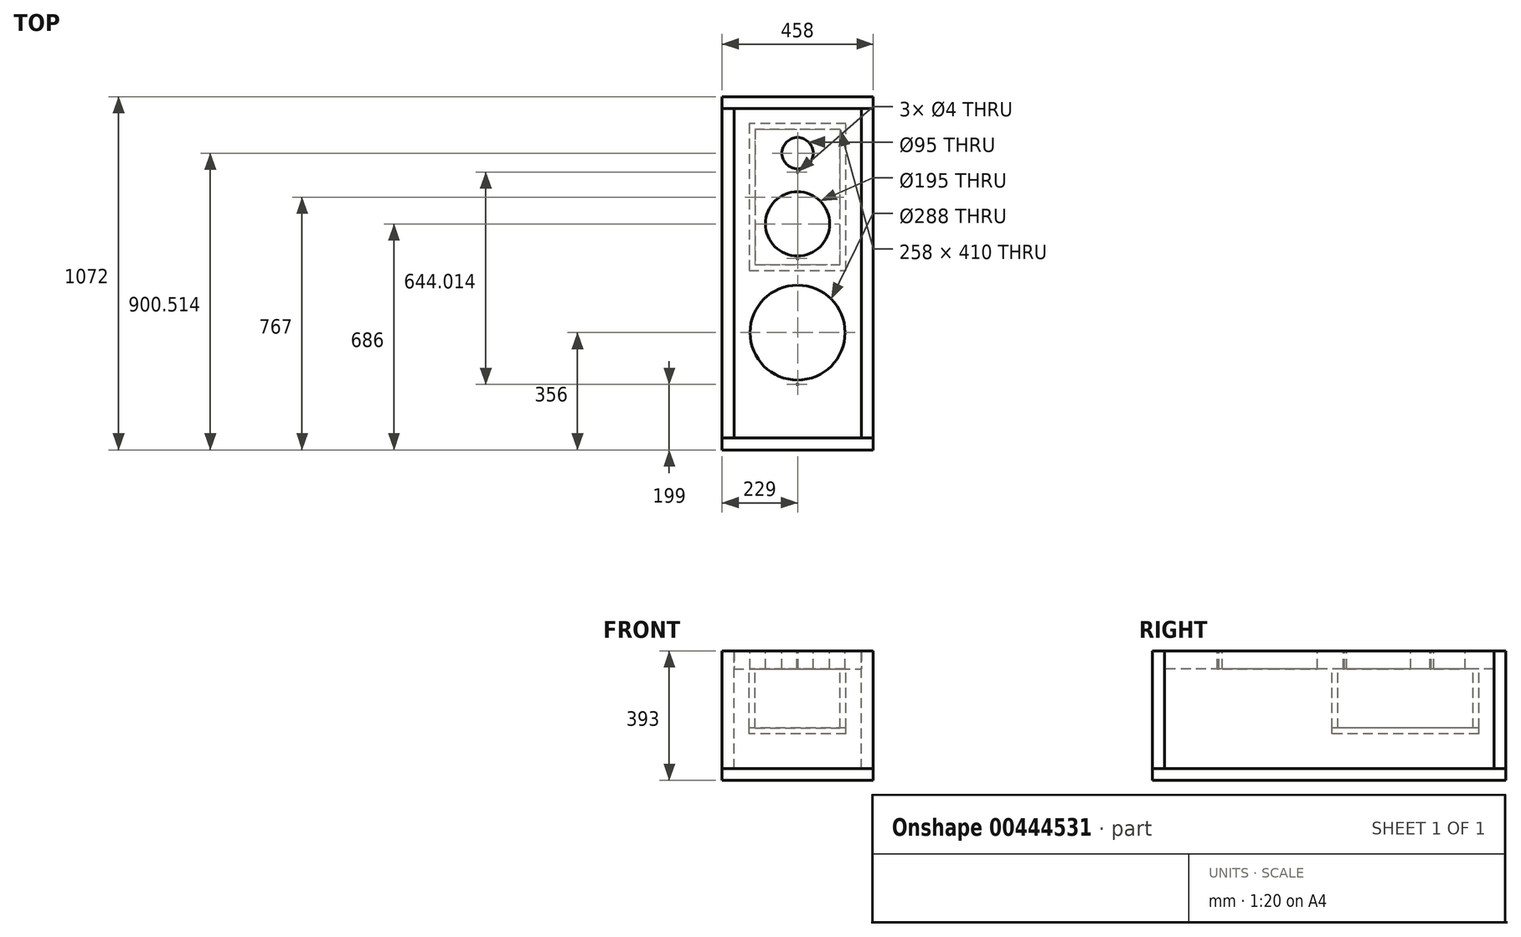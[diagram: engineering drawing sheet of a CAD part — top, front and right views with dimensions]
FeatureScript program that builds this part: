
annotation { "Feature Type Name" : "Feature", "Feature Type Description" : "" }
export const myFeature = defineFeature(function(context is Context, id is Id, definition is map)
    precondition{}
    {
        {
            var Q0;
            Q0=qCreatedBy(makeId("Top.planeOp"),FACE);
            var sketch = newSketch(context, id + "F0", { "sketchPlane" : qUnion([Q0])});
            skLineSegment(sketch, "E0.bottom", {"start": v(-193, 500) * mm, "end": v(193, 500) * mm});
            skLineSegment(sketch, "E0.top", {"start": v(-193, -500) * mm, "end": v(193, -500) * mm});
            skLineSegment(sketch, "E0.left", {"start": v(-193, 500) * mm, "end": v(-193, -500) * mm});
            skLineSegment(sketch, "E0.right", {"start": v(193, 500) * mm, "end": v(193, -500) * mm});
            skPoint(sketch, "E0.middle", {"position": v(0, 0) * mm});
            skSolve(sketch);
        }
        {
            var Q0;
            Q0 = qSketchRegion(id + "F0", true);
            extrude(context, id + "F1", {"entities" : qUnion([Q0]), "depth" : 54 * mm});
        }
        {
            var Q0;
            Q0=makeQuery(id+"F1.opExtrude","CAP_FACE",FACE,{"disambiguationData":[OSD([sQuery(id+"F0.wireOp",EDGE,"E0.bottom"),sQuery(id+"F0.wireOp",EDGE,"E0.top"),sQuery(id+"F0.wireOp",EDGE,"E0.left"),sQuery(id+"F0.wireOp",EDGE,"E0.right")])],"isStart":false});
            var sketch = newSketch(context, id + "F2", { "sketchPlane" : qUnion([Q0])});
            skCircle(sketch, "E1", {"center": v(0, -180) * mm, "radius": 144 * mm});
            skCircle(sketch, "E2", {"center": v(0, 150) * mm, "radius": 97.5 * mm});
            skCircle(sketch, "E3", {"center": v(0, 364.51) * mm, "radius": 47.5 * mm});
            skSolve(sketch);
        }
        {
            var Q0;
            Q0 = qSketchRegion(id + "F2", true);
            extrude(context, id + "F3", {"entities" : qUnion([Q0]), "operationType" : NewBodyOperationType.REMOVE, "oppositeDirection" : true, "depth" : 80 * mm});
        }
        {
            var Q0;
            Q0=makeQuery(id+"F1.opExtrude","SWEPT_FACE",FACE,{"disambiguationData":[OSD([sQuery(id+"F0.wireOp",EDGE,"E0.left")])]});
            var sketch = newSketch(context, id + "F4", { "sketchPlane" : qUnion([Q0])});
            skLineSegment(sketch, "E4", {"start": v(-500, 54) * mm, "end": v(-500, -303) * mm});
            skLineSegment(sketch, "E5", {"start": v(-500, -303) * mm, "end": v(500, -303) * mm});
            skLineSegment(sketch, "E6", {"start": v(500, -303) * mm, "end": v(500, 54) * mm});
            skLineSegment(sketch, "E7", {"start": v(500, 54) * mm, "end": v(-500, 54) * mm});
            skSolve(sketch);
        }
        {
            var Q0;
            Q0 = qSketchRegion(id + "F4", true);
            extrude(context, id + "F5", {"entities" : qUnion([Q0]), "depth" : 36 * mm});
        }
        {
            var Q0;
            Q0=makeQuery(id+"F1.opExtrude","SWEPT_FACE",FACE,{"disambiguationData":[OSD([sQuery(id+"F0.wireOp",EDGE,"E0.right")])]});
            var sketch = newSketch(context, id + "F6", { "sketchPlane" : qUnion([Q0])});
            skLineSegment(sketch, "E8", {"start": v(-500, 54) * mm, "end": v(-500, -303) * mm});
            skPoint(sketch, "E8.endSnap0", {"position": v(-500, 27) * mm});
            skLineSegment(sketch, "E9", {"start": v(-500, -303) * mm, "end": v(500, -303) * mm});
            skLineSegment(sketch, "E10", {"start": v(500, -303) * mm, "end": v(500, 54) * mm});
            skLineSegment(sketch, "E11", {"start": v(500, 54) * mm, "end": v(-500, 54) * mm});
            skSolve(sketch);
        }
        {
            var Q0;
            Q0 = qSketchRegion(id + "F6", true);
            extrude(context, id + "F7", {"entities" : qUnion([Q0]), "depth" : 36 * mm});
        }
        {
            var Q0;
            Q0=makeQuery(id+"F1.opExtrude","CAP_FACE",FACE,{"disambiguationData":[OSD([sQuery(id+"F0.wireOp",EDGE,"E0.bottom"),sQuery(id+"F0.wireOp",EDGE,"E0.top"),sQuery(id+"F0.wireOp",EDGE,"E0.left"),sQuery(id+"F0.wireOp",EDGE,"E0.right")])],"isStart":true});
            var sketch = newSketch(context, id + "F8", { "sketchPlane" : qUnion([Q0])});
            skLineSegment(sketch, "E12", {"start": v(-129, -26) * mm, "end": v(129, -26) * mm});
            skLineSegment(sketch, "E13", {"start": v(129, -26) * mm, "end": v(129, -436) * mm});
            skLineSegment(sketch, "E14", {"start": v(129, -436) * mm, "end": v(-129, -436) * mm});
            skLineSegment(sketch, "E15", {"start": v(-129, -436) * mm, "end": v(-129, -26) * mm});
            skLineSegment(sketch, "E16.0", {"start": v(-147, -454) * mm, "end": v(-147, -8) * mm});
            skLineSegment(sketch, "E16.1", {"start": v(147, -454) * mm, "end": v(-147, -454) * mm});
            skLineSegment(sketch, "E16.2", {"start": v(147, -8) * mm, "end": v(147, -454) * mm});
            skLineSegment(sketch, "E16.3", {"start": v(-147, -8) * mm, "end": v(147, -8) * mm});
            skSolve(sketch);
        }
        {
            var Q0;
            Q0=makeQuery(id+"F8.imprint","IMPRINT",FACE,{"disambiguationData":[TD([[makeQuery(id+"F8.imprint","IMPRINT",EDGE,{"derivedFrom":sQuery(id+"F8.wireOp",EDGE,"E12")}),1.0]])]});
            extrude(context, id + "F9", {"entities" : qUnion([Q0]), "depth" : 180 * mm});
        }
        {
            var Q0;
            Q0=makeQuery(id+"F9.opExtrude","CAP_FACE",FACE,{"disambiguationData":[OSD([sQuery(id+"F8.wireOp",EDGE,"E12"),sQuery(id+"F8.wireOp",EDGE,"E13"),sQuery(id+"F8.wireOp",EDGE,"E14"),sQuery(id+"F8.wireOp",EDGE,"E15"),sQuery(id+"F8.wireOp",EDGE,"E16.0"),sQuery(id+"F8.wireOp",EDGE,"E16.1"),sQuery(id+"F8.wireOp",EDGE,"E16.2"),sQuery(id+"F8.wireOp",EDGE,"E16.3")])],"isStart":false});
            var sketch = newSketch(context, id + "F10", { "sketchPlane" : qUnion([Q0])});
            skLineSegment(sketch, "E17", {"start": v(-147, -8) * mm, "end": v(147, -8) * mm});
            skLineSegment(sketch, "E18", {"start": v(147, -8) * mm, "end": v(147, -454) * mm});
            skLineSegment(sketch, "E19", {"start": v(147, -454) * mm, "end": v(-147, -454) * mm});
            skLineSegment(sketch, "E20", {"start": v(-147, -454) * mm, "end": v(-147, -8) * mm});
            skSolve(sketch);
        }
        {
            var Q0;
            Q0 = qSketchRegion(id + "F10", true);
            extrude(context, id + "F11", {"entities" : qUnion([Q0]), "depth" : 18 * mm});
        }
        {
            var Q0;
            Q0=makeQuery(id+"F1.opExtrude","SWEPT_FACE",FACE,{"disambiguationData":[OSD([sQuery(id+"F0.wireOp",EDGE,"E0.bottom")])]});
            var sketch = newSketch(context, id + "F12", { "sketchPlane" : qUnion([Q0])});
            skLineSegment(sketch, "E21", {"start": v(-229, 54) * mm, "end": v(229, 54) * mm});
            skLineSegment(sketch, "E22", {"start": v(229, 54) * mm, "end": v(229, -303) * mm});
            skLineSegment(sketch, "E23", {"start": v(229, -303) * mm, "end": v(-229, -303) * mm});
            skLineSegment(sketch, "E24", {"start": v(-229, -303) * mm, "end": v(-229, 54) * mm});
            skSolve(sketch);
        }
        {
            var Q0;
            Q0 = qSketchRegion(id + "F12", true);
            extrude(context, id + "F13", {"entities" : qUnion([Q0]), "depth" : 36 * mm});
        }
        {
            var Q0;
            Q0=makeQuery(id+"F1.opExtrude","SWEPT_FACE",FACE,{"disambiguationData":[OSD([sQuery(id+"F0.wireOp",EDGE,"E0.top")])]});
            var sketch = newSketch(context, id + "F14", { "sketchPlane" : qUnion([Q0])});
            skLineSegment(sketch, "E25", {"start": v(-229, 54) * mm, "end": v(229, 54) * mm});
            skLineSegment(sketch, "E26", {"start": v(229, 54) * mm, "end": v(229, -303) * mm});
            skLineSegment(sketch, "E27", {"start": v(229, -303) * mm, "end": v(-229, -303) * mm});
            skLineSegment(sketch, "E28", {"start": v(-229, -303) * mm, "end": v(-229, 54) * mm});
            skSolve(sketch);
        }
        {
            var Q0;
            Q0 = qSketchRegion(id + "F14", true);
            extrude(context, id + "F15", {"entities" : qUnion([Q0]), "depth" : 36 * mm});
        }
        {
            var Q0;
            Q0=makeQuery(id+"F15.opExtrude","SWEPT_FACE",FACE,{"disambiguationData":[OSD([sQuery(id+"F14.wireOp",EDGE,"E27")])]});
            var sketch = newSketch(context, id + "F16", { "sketchPlane" : qUnion([Q0])});
            skLineSegment(sketch, "E29", {"start": v(-229, 536) * mm, "end": v(229, 536) * mm});
            skLineSegment(sketch, "E30", {"start": v(229, 536) * mm, "end": v(229, -536) * mm});
            skLineSegment(sketch, "E31", {"start": v(229, -536) * mm, "end": v(-229, -536) * mm});
            skLineSegment(sketch, "E32", {"start": v(-229, -536) * mm, "end": v(-229, 536) * mm});
            skSolve(sketch);
        }
        {
            var Q0;
            Q0 = qSketchRegion(id + "F16", true);
            extrude(context, id + "F17", {"entities" : qUnion([Q0]), "depth" : 36 * mm});
        }
        {
            var Q0;
            Q0=makeQuery(id+"F1.opExtrude","CAP_FACE",FACE,{"disambiguationData":[OSD([sQuery(id+"F0.wireOp",EDGE,"E0.bottom"),sQuery(id+"F0.wireOp",EDGE,"E0.top"),sQuery(id+"F0.wireOp",EDGE,"E0.left"),sQuery(id+"F0.wireOp",EDGE,"E0.right")])],"isStart":false});
            var sketch = newSketch(context, id + "F18", { "sketchPlane" : qUnion([Q0])});
            skCircle(sketch, "E33", {"center": v(0, -180) * mm, "radius": 157 * mm});
            skPoint(sketch, "E34", {"position": v(0, -337) * mm});
            skPoint(sketch, "E35", {"position": v(-434.74, 564.77) * mm});
            skSolve(sketch);
        }
        {
            var Q0;
            Q0=sQuery(id+"F18.wireOp",VERTEX,"E34");
            var Q1;
            Q1=makeQuery(id+"F1.opExtrude","SWEPT_BODY",BODY,{"disambiguationData":[OSD([sQuery(id+"F0.wireOp",EDGE,"E0.bottom"),sQuery(id+"F0.wireOp",EDGE,"E0.top"),sQuery(id+"F0.wireOp",EDGE,"E0.left"),sQuery(id+"F0.wireOp",EDGE,"E0.right")])]});
            hole(context, id + "F19", {"style" : HoleStyle.SIMPLE, "endStyle" : HoleEndStyle.THROUGH, "holeDiameter" : 4 * mm, "isTappedThrough" : true, "tappedDepth" : 12 * mm, "tapClearance" : 3, "locations" : qUnion([Q0]), "scope" : qUnion([Q1])});
        }
        {
            var Q0;
            Q0=makeQuery(id+"F1.opExtrude","CAP_FACE",FACE,{"disambiguationData":[OSD([sQuery(id+"F0.wireOp",EDGE,"E0.bottom"),sQuery(id+"F0.wireOp",EDGE,"E0.top"),sQuery(id+"F0.wireOp",EDGE,"E0.left"),sQuery(id+"F0.wireOp",EDGE,"E0.right")])],"isStart":false});
            var sketch = newSketch(context, id + "F20", { "sketchPlane" : qUnion([Q0])});
            skCircle(sketch, "E36", {"center": v(0, 150) * mm, "radius": 105 * mm});
            skCircle(sketch, "E37", {"center": v(0, 364.51) * mm, "radius": 57.5 * mm});
            skPoint(sketch, "E38", {"position": v(0, 45) * mm});
            skPoint(sketch, "E39", {"position": v(0, 307.01) * mm});
            skSolve(sketch);
        }
        {
            var Q0;
            Q0=sQuery(id+"F20.wireOp",VERTEX,"E38");
            var Q1;
            Q1=makeQuery(id+"F1.opExtrude","SWEPT_BODY",BODY,{"disambiguationData":[OSD([sQuery(id+"F0.wireOp",EDGE,"E0.bottom"),sQuery(id+"F0.wireOp",EDGE,"E0.top"),sQuery(id+"F0.wireOp",EDGE,"E0.left"),sQuery(id+"F0.wireOp",EDGE,"E0.right")])]});
            hole(context, id + "F21", {"style" : HoleStyle.SIMPLE, "endStyle" : HoleEndStyle.THROUGH, "holeDiameter" : 4 * mm, "isTappedThrough" : true, "tappedDepth" : 12 * mm, "tapClearance" : 3, "locations" : qUnion([Q0]), "scope" : qUnion([Q1])});
        }
        {
            var Q0;
            Q0=makeQuery(id+"F1.opExtrude","CAP_FACE",FACE,{"disambiguationData":[OSD([sQuery(id+"F0.wireOp",EDGE,"E0.bottom"),sQuery(id+"F0.wireOp",EDGE,"E0.top"),sQuery(id+"F0.wireOp",EDGE,"E0.left"),sQuery(id+"F0.wireOp",EDGE,"E0.right")])],"isStart":false});
            var sketch = newSketch(context, id + "F22", { "sketchPlane" : qUnion([Q0])});
            skCircle(sketch, "E40", {"center": v(0, 364.51) * mm, "radius": 57.5 * mm});
            skPoint(sketch, "E41", {"position": v(0, 307.01) * mm});
            skSolve(sketch);
        }
        {
            var Q0;
            Q0=sQuery(id+"F22.wireOp",VERTEX,"E41");
            var Q1;
            Q1=makeQuery(id+"F1.opExtrude","SWEPT_BODY",BODY,{"disambiguationData":[OSD([sQuery(id+"F0.wireOp",EDGE,"E0.bottom"),sQuery(id+"F0.wireOp",EDGE,"E0.top"),sQuery(id+"F0.wireOp",EDGE,"E0.left"),sQuery(id+"F0.wireOp",EDGE,"E0.right")])]});
            hole(context, id + "F23", {"style" : HoleStyle.SIMPLE, "endStyle" : HoleEndStyle.THROUGH, "holeDiameter" : 4 * mm, "isTappedThrough" : true, "tappedDepth" : 12 * mm, "tapClearance" : 3, "locations" : qUnion([Q0]), "scope" : qUnion([Q1])});
        }
    });
